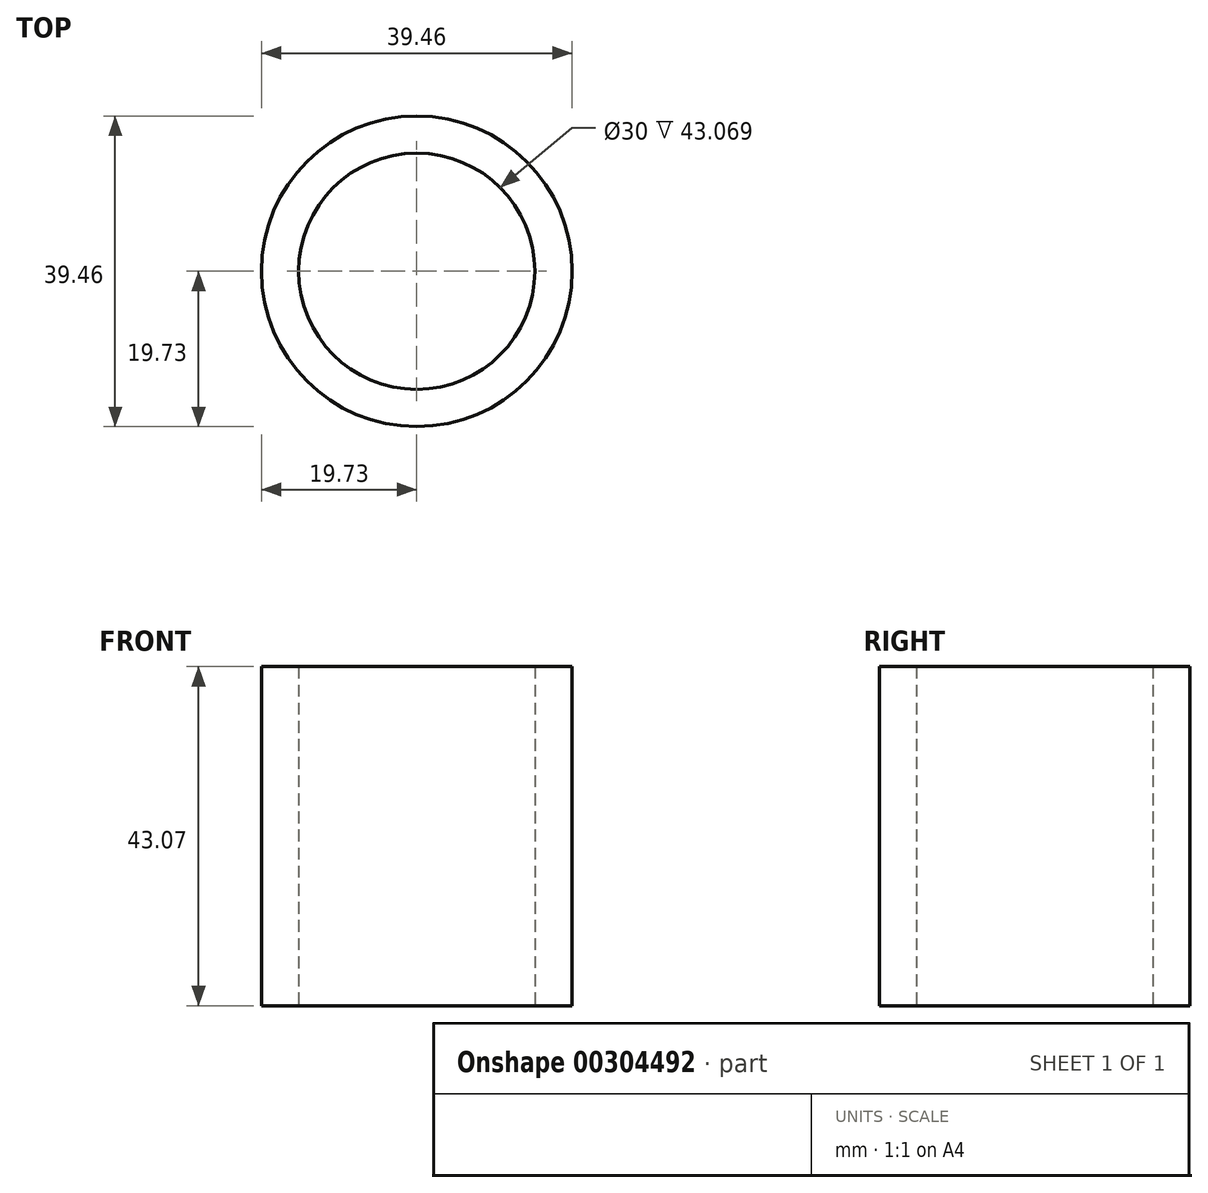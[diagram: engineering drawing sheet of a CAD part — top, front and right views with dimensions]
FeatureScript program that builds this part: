
annotation { "Feature Type Name" : "Feature", "Feature Type Description" : "" }
export const myFeature = defineFeature(function(context is Context, id is Id, definition is map)
    precondition{}
    {
        {
            var Q0;
            Q0=qCreatedBy(makeId("Right.planeOp"),FACE);
            var sketch = newSketch(context, id + "F0", { "sketchPlane" : qUnion([Q0])});
            skLineSegment(sketch, "E0", {"start": v(0, 0) * mm, "end": v(0, 100) * mm, "construction": true});
            skLineSegment(sketch, "E1", {"start": v(15, 100) * mm, "end": v(15, 143.07) * mm});
            skLineSegment(sketch, "E2", {"start": v(15, 143.07) * mm, "end": v(19.73, 143.07) * mm});
            skLineSegment(sketch, "E3", {"start": v(19.73, 143.07) * mm, "end": v(19.73, 100) * mm});
            skLineSegment(sketch, "E4", {"start": v(19.73, 100) * mm, "end": v(15, 100) * mm});
            skSolve(sketch);
        }
        {
            var Q0;
            Q0=makeQuery(id+"F0.imprint","IMPRINT",FACE,{"disambiguationData":[TD([[makeQuery(id+"F0.imprint","IMPRINT",EDGE,{"derivedFrom":sQuery(id+"F0.wireOp",EDGE,"E1")}),-1.0]])]});
            var Q1;
            Q1=sQuery(id+"F0.wireOp",EDGE,"E0");
            revolve(context, id + "F1", {"entities" : qUnion([Q0]), "axis" : qUnion([Q1]), "revolveType" : RevolveType.FULL});
        }
    });
